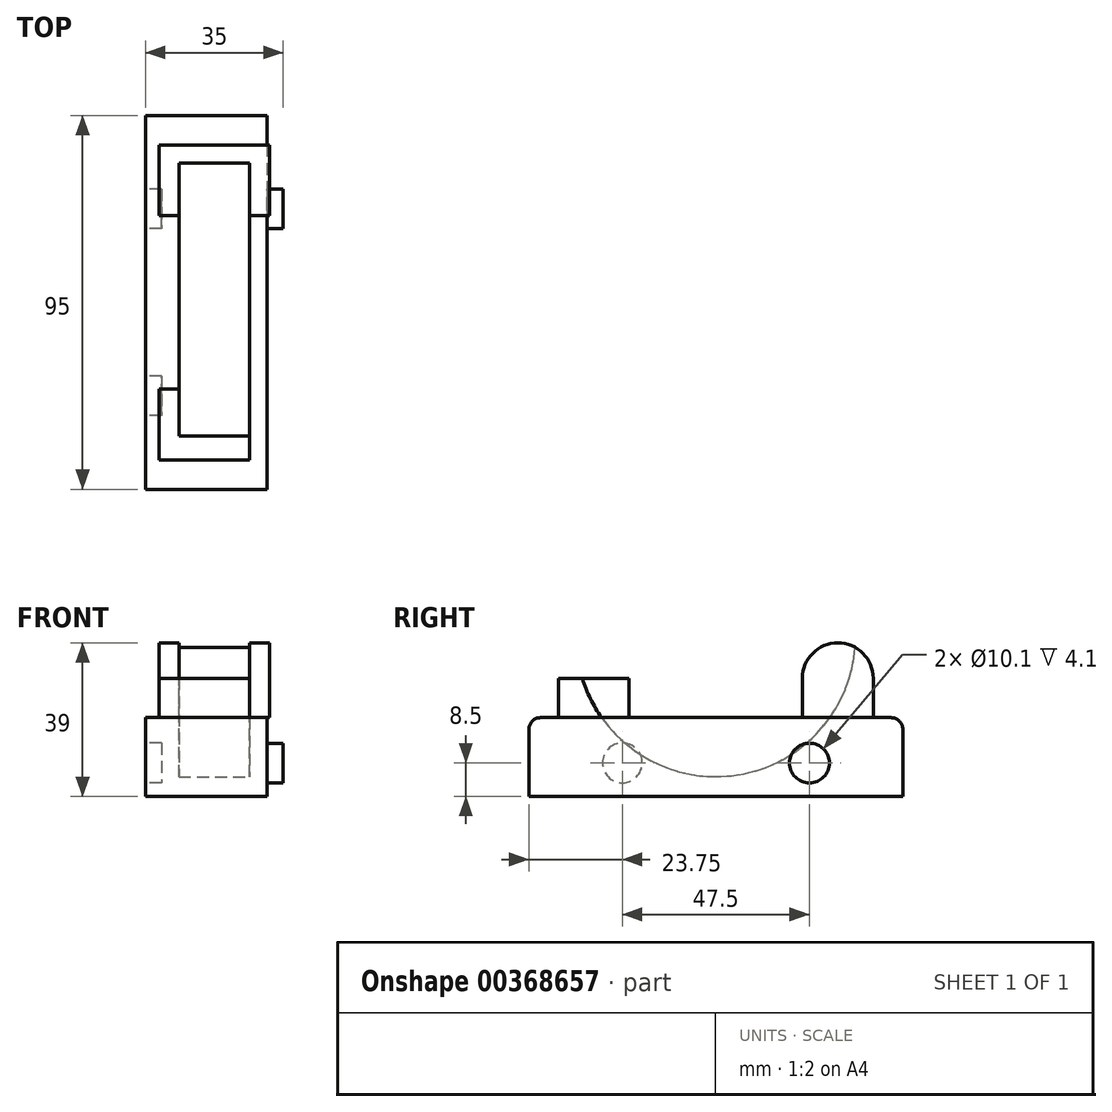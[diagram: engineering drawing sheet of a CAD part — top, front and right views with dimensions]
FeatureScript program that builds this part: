
annotation { "Feature Type Name" : "Feature", "Feature Type Description" : "" }
export const myFeature = defineFeature(function(context is Context, id is Id, definition is map)
    precondition{}
    {
        {
            var Q0;
            Q0=qCreatedBy(makeId("Top.planeOp"),FACE);
            var sketch = newSketch(context, id + "F0", { "sketchPlane" : qUnion([Q0])});
            skLineSegment(sketch, "E0.bottom", {"start": v(17.5, 47.5) * mm, "end": v(-17.5, 47.5) * mm});
            skLineSegment(sketch, "E0.top", {"start": v(17.5, -47.5) * mm, "end": v(-17.5, -47.5) * mm});
            skLineSegment(sketch, "E0.left", {"start": v(17.5, 47.5) * mm, "end": v(17.5, -47.5) * mm});
            skLineSegment(sketch, "E0.right", {"start": v(-17.5, 47.5) * mm, "end": v(-17.5, -47.5) * mm});
            skPoint(sketch, "E0.middle", {"position": v(0, 0) * mm});
            skSolve(sketch);
        }
        {
            var Q0;
            Q0=makeQuery(id+"F0.imprint","IMPRINT",FACE,{"disambiguationData":[TD([[makeQuery(id+"F0.imprint","IMPRINT",EDGE,{"derivedFrom":sQuery(id+"F0.wireOp",EDGE,"E0.bottom")}),1.0]])]});
            extrude(context, id + "F1", {"entities" : qUnion([Q0]), "depth" : 20 * mm});
        }
        {
            var Q0;
            Q0=makeQuery(id+"F1.opExtrude","CAP_FACE",FACE,{"disambiguationData":[OSD([sQuery(id+"F0.wireOp",EDGE,"E0.bottom"),sQuery(id+"F0.wireOp",EDGE,"E0.top"),sQuery(id+"F0.wireOp",EDGE,"E0.left"),sQuery(id+"F0.wireOp",EDGE,"E0.right")])],"isStart":false});
            var sketch = newSketch(context, id + "F2", { "sketchPlane" : qUnion([Q0])});
            skLineSegment(sketch, "E1.bottom", {"start": v(14, 40) * mm, "end": v(-14, 40) * mm});
            skLineSegment(sketch, "E1.top", {"start": v(14, -40) * mm, "end": v(-14, -40) * mm});
            skLineSegment(sketch, "E1.left", {"start": v(14, 40) * mm, "end": v(14, -40) * mm});
            skLineSegment(sketch, "E1.right", {"start": v(-14, 40) * mm, "end": v(-14, -40) * mm});
            skPoint(sketch, "E1.middle", {"position": v(0, 0) * mm});
            skLineSegment(sketch, "E2.bottom", {"start": v(14, -40) * mm, "end": v(9, -40) * mm});
            skLineSegment(sketch, "E2.top", {"start": v(14, -22) * mm, "end": v(9, -22) * mm});
            skLineSegment(sketch, "E2.left", {"start": v(14, -40) * mm, "end": v(14, -22) * mm});
            skLineSegment(sketch, "E2.right", {"start": v(9, -40) * mm, "end": v(9, -22) * mm});
            skLineSegment(sketch, "E3", {"start": v(0, 0) * mm, "end": v(4.01, 0) * mm, "construction": true});
            skLineSegment(sketch, "E4", {"start": v(0, 4.8) * mm, "end": v(0, -5.54) * mm, "construction": true});
            skLineSegment(sketch, "E5.MirrorCS", {"start": v(-9, -40) * mm, "end": v(-9, -22) * mm});
            skLineSegment(sketch, "E6.MirrorCS", {"start": v(-14, -22) * mm, "end": v(-9, -22) * mm});
            skLineSegment(sketch, "E7.MirrorCS", {"start": v(14, 22) * mm, "end": v(9, 22) * mm});
            skLineSegment(sketch, "E8.MirrorCS", {"start": v(9, 40) * mm, "end": v(9, 22) * mm});
            skLineSegment(sketch, "E9.MirrorCS", {"start": v(-9, 40) * mm, "end": v(-9, 22) * mm});
            skLineSegment(sketch, "E10.MirrorCS", {"start": v(-14, 22) * mm, "end": v(-9, 22) * mm});
            skLineSegment(sketch, "E11", {"start": v(-9, -22) * mm, "end": v(9, -22) * mm});
            skLineSegment(sketch, "E12", {"start": v(9, 22) * mm, "end": v(-9, 22) * mm});
            skSolve(sketch);
        }
        {
            var Q0;
            {var subQ3=sQuery(id+"F2.wireOp",EDGE,"E5.MirrorCS");Q0=makeQuery(id+"F2.imprint","IMPRINT",FACE,{"disambiguationData":[TD([[makeQuery(id+"F2.imprint","IMPRINT",EDGE,{"derivedFrom":subQ3}),1.0]])]});}
            var Q1;
            Q1=makeQuery(id+"F2.imprint","IMPRINT",FACE,{"disambiguationData":[TD([[makeQuery(id+"F2.imprint","IMPRINT",EDGE,{"derivedFrom":sQuery(id+"F2.wireOp",EDGE,"E2.bottom")}),-1.0]])]});
            var Q2;
            {var subQ4=sQuery(id+"F2.wireOp",EDGE,"E7.MirrorCS");Q2=makeQuery(id+"F2.imprint","IMPRINT",FACE,{"disambiguationData":[TD([[makeQuery(id+"F2.imprint","IMPRINT",EDGE,{"derivedFrom":subQ4}),-1.0]])]});}
            var Q3;
            {var subQ3=sQuery(id+"F2.wireOp",EDGE,"E9.MirrorCS");Q3=makeQuery(id+"F2.imprint","IMPRINT",FACE,{"disambiguationData":[TD([[makeQuery(id+"F2.imprint","IMPRINT",EDGE,{"derivedFrom":subQ3}),-1.0]])]});}
            var Q4;
            {var subQ0=sQuery(id+"F2.wireOp",EDGE,"E2.right");Q4=makeQuery(id+"F2.imprint","IMPRINT",FACE,{"disambiguationData":[TD([[makeQuery(id+"F2.imprint","IMPRINT",EDGE,{"derivedFrom":subQ0}),1.0]])]});}
            var Q5;
            {var subQ0=sQuery(id+"F2.wireOp",EDGE,"E8.MirrorCS");Q5=makeQuery(id+"F2.imprint","IMPRINT",FACE,{"disambiguationData":[TD([[makeQuery(id+"F2.imprint","IMPRINT",EDGE,{"derivedFrom":subQ0}),-1.0]])]});}
            extrude(context, id + "F3", {"entities" : qUnion([Q0, Q1, Q2, Q3, Q4, Q5]), "operationType" : NewBodyOperationType.ADD, "depth" : 10 * mm});
        }
        {
            var Q0;
            Q0=makeQuery(id+"F3.opExtrude","SWEPT_FACE",FACE,{"disambiguationData":[OSD([sQuery(id+"F2.wireOp",EDGE,"E1.left")])]});
            var sketch = newSketch(context, id + "F4", { "sketchPlane" : qUnion([Q0])});
            skArc(sketch, "E13", {"start": v(40, 30) * mm, "mid": v(31, 39) * mm, "end": v(22, 30) * mm});
            skSolve(sketch);
        }
        {
            var Q0;
            Q0=makeQuery(id+"F3.opExtrude","SWEPT_FACE",FACE,{"disambiguationData":[OSD([sQuery(id+"F2.wireOp",EDGE,"E2.left")])]});
            var sketch = newSketch(context, id + "F5", { "sketchPlane" : qUnion([Q0])});
            skArc(sketch, "E14", {"start": v(-22, 30) * mm, "mid": v(-31, 39) * mm, "end": v(-40, 30) * mm});
            skSolve(sketch);
        }
        {
            var Q0;
            Q0=makeQuery(id+"F5.imprint","IMPRINT",FACE,{"disambiguationData":[TD([[makeQuery(id+"F5.imprint","IMPRINT",EDGE,{"derivedFrom":sQuery(id+"F5.wireOp",EDGE,"E14")}),1.0]])]});
            var Q1;
            Q1=makeQuery(id+"F4.imprint","IMPRINT",FACE,{"disambiguationData":[TD([[makeQuery(id+"F4.imprint","IMPRINT",EDGE,{"derivedFrom":sQuery(id+"F4.wireOp",EDGE,"E13")}),1.0]])]});
            extrude(context, id + "F6", {"entities" : qUnion([Q0, Q1]), "operationType" : NewBodyOperationType.ADD, "oppositeDirection" : true, "depth" : 28 * mm});
        }
        {
            var Q0;
            Q0=qCreatedBy(makeId("Right.planeOp"),FACE);
            var sketch = newSketch(context, id + "F7", { "sketchPlane" : qUnion([Q0])});
            skCircle(sketch, "E15", {"center": v(0, 40.5) * mm, "radius": 35.5 * mm});
            skLineSegment(sketch, "E16", {"start": v(0, 40.5) * mm, "end": v(-35.5, 40.5) * mm, "construction": true});
            skLineSegment(sketch, "E17", {"start": v(0, 40.5) * mm, "end": v(35.5, 40.5) * mm, "construction": true});
            skLineSegment(sketch, "E18.bottom", {"start": v(-35.5, 40.5) * mm, "end": v(35.5, 40.5) * mm});
            skLineSegment(sketch, "E19.top", {"start": v(-35.5, 76) * mm, "end": v(35.5, 76) * mm});
            skLineSegment(sketch, "E19.left", {"start": v(-35.5, 40.5) * mm, "end": v(-35.5, 76) * mm});
            skLineSegment(sketch, "E19.right", {"start": v(35.5, 40.5) * mm, "end": v(35.5, 76) * mm});
            skSolve(sketch);
        }
        {
            var Q0;
            Q0=makeQuery(id+"F7.imprint","IMPRINT",FACE,{"disambiguationData":[TD([[makeQuery(id+"F7.imprint","IMPRINT",EDGE,{"derivedFrom":sQuery(id+"F7.wireOp",EDGE,"E15")}),1.0]])]});
            var Q1;
            {var subQ0=sQuery(id+"F7.wireOp",EDGE,"E19.left");Q1=makeQuery(id+"F7.imprint","IMPRINT",FACE,{"disambiguationData":[TD([[makeQuery(id+"F7.imprint","IMPRINT",EDGE,{"derivedFrom":subQ0}),-1.0]])]});}
            var Q2;
            {var subQ0=sQuery(id+"F7.wireOp",EDGE,"E19.right");Q2=makeQuery(id+"F7.imprint","IMPRINT",FACE,{"disambiguationData":[TD([[makeQuery(id+"F7.imprint","IMPRINT",EDGE,{"derivedFrom":subQ0}),1.0]])]});}
            var Q3;
            {var subQ0=sQuery(id+"F7.wireOp",EDGE,"E18.bottom");Q3=makeQuery(id+"F7.imprint","IMPRINT",FACE,{"disambiguationData":[TD([[makeQuery(id+"F7.imprint","IMPRINT",EDGE,{"derivedFrom":subQ0}),-1.0]])]});}
            extrude(context, id + "F8", {"entities" : qUnion([Q0, Q1, Q2, Q3]), "operationType" : NewBodyOperationType.REMOVE, "endBound" : BoundingType.SYMMETRIC, "oppositeDirection" : true, "depth" : 18 * mm});
        }
        {
            var Q0;
            Q0=makeQuery(id+"F1.opExtrude","CAP_EDGE",EDGE,{"disambiguationData":[OSD([sQuery(id+"F0.wireOp",EDGE,"E0.top")])],"isStart":false});
            var Q1;
            Q1=makeQuery(id+"F1.opExtrude","CAP_EDGE",EDGE,{"disambiguationData":[OSD([sQuery(id+"F0.wireOp",EDGE,"E0.bottom")])],"isStart":false});
            fillet(context, id + "F9", {"entities" : qUnion([Q0, Q1]), "radius" : 3 * mm, "tangentPropagation" : true, "allowEdgeOverflow" : false});
        }
        {
            var Q0;
            Q0=makeQuery(id+"F1.opExtrude","SWEPT_FACE",FACE,{"disambiguationData":[OSD([sQuery(id+"F0.wireOp",EDGE,"E0.left")])]});
            var sketch = newSketch(context, id + "F10", { "sketchPlane" : qUnion([Q0])});
            skPoint(sketch, "E20", {"position": v(-23.8, 8.45) * mm});
            skCircle(sketch, "E21", {"center": v(-23.8, 8.45) * mm, "radius": 5.05 * mm});
            skCircle(sketch, "E22.MirrorC", {"center": v(23.8, 8.45) * mm, "radius": 5.05 * mm});
            skSolve(sketch);
        }
        {
            var Q0;
            Q0=makeQuery(id+"F10.imprint","IMPRINT",FACE,{"disambiguationData":[TD([[makeQuery(id+"F10.imprint","IMPRINT",EDGE,{"derivedFrom":sQuery(id+"F10.wireOp",EDGE,"E21")}),1.0]])]});
            var Q1;
            Q1=makeQuery(id+"F10.imprint","IMPRINT",FACE,{"disambiguationData":[TD([[makeQuery(id+"F10.imprint","IMPRINT",EDGE,{"derivedFrom":sQuery(id+"F10.wireOp",EDGE,"E22.MirrorC")}),-1.0]])]});
            var Q2;
            Q2=sQuery(id+"F10.wireOp",EDGE,"E21");
            var Q3;
            Q3=sQuery(id+"F10.wireOp",EDGE,"E22.MirrorC");
            extrude(context, id + "F11", {"entities" : qUnion([Q0, Q1]), "operationType" : NewBodyOperationType.REMOVE, "surfaceEntities" : qUnion([Q2, Q3]), "oppositeDirection" : true, "depth" : 4.1 * mm});
        }
        {
            var Q0;
            Q0=makeQuery(id+"F1.opExtrude","SWEPT_FACE",FACE,{"disambiguationData":[OSD([sQuery(id+"F0.wireOp",EDGE,"E0.right")])]});
            var sketch = newSketch(context, id + "F12", { "sketchPlane" : qUnion([Q0])});
            skLineSegment(sketch, "E23", {"start": v(-47.5, 8.5) * mm, "end": v(0, 8.5) * mm, "construction": true});
            skCircle(sketch, "E24", {"center": v(-23.75, 8.5) * mm, "radius": 5.05 * mm});
            skCircle(sketch, "E25.MirrorC", {"center": v(23.75, 8.5) * mm, "radius": 5.05 * mm});
            skSolve(sketch);
        }
        {
            var Q0;
            Q0 = qSketchRegion(id + "F12", true);
            extrude(context, id + "F13", {"entities" : qUnion([Q0]), "operationType" : NewBodyOperationType.REMOVE, "oppositeDirection" : true, "depth" : 4.1 * mm});
        }
    });
